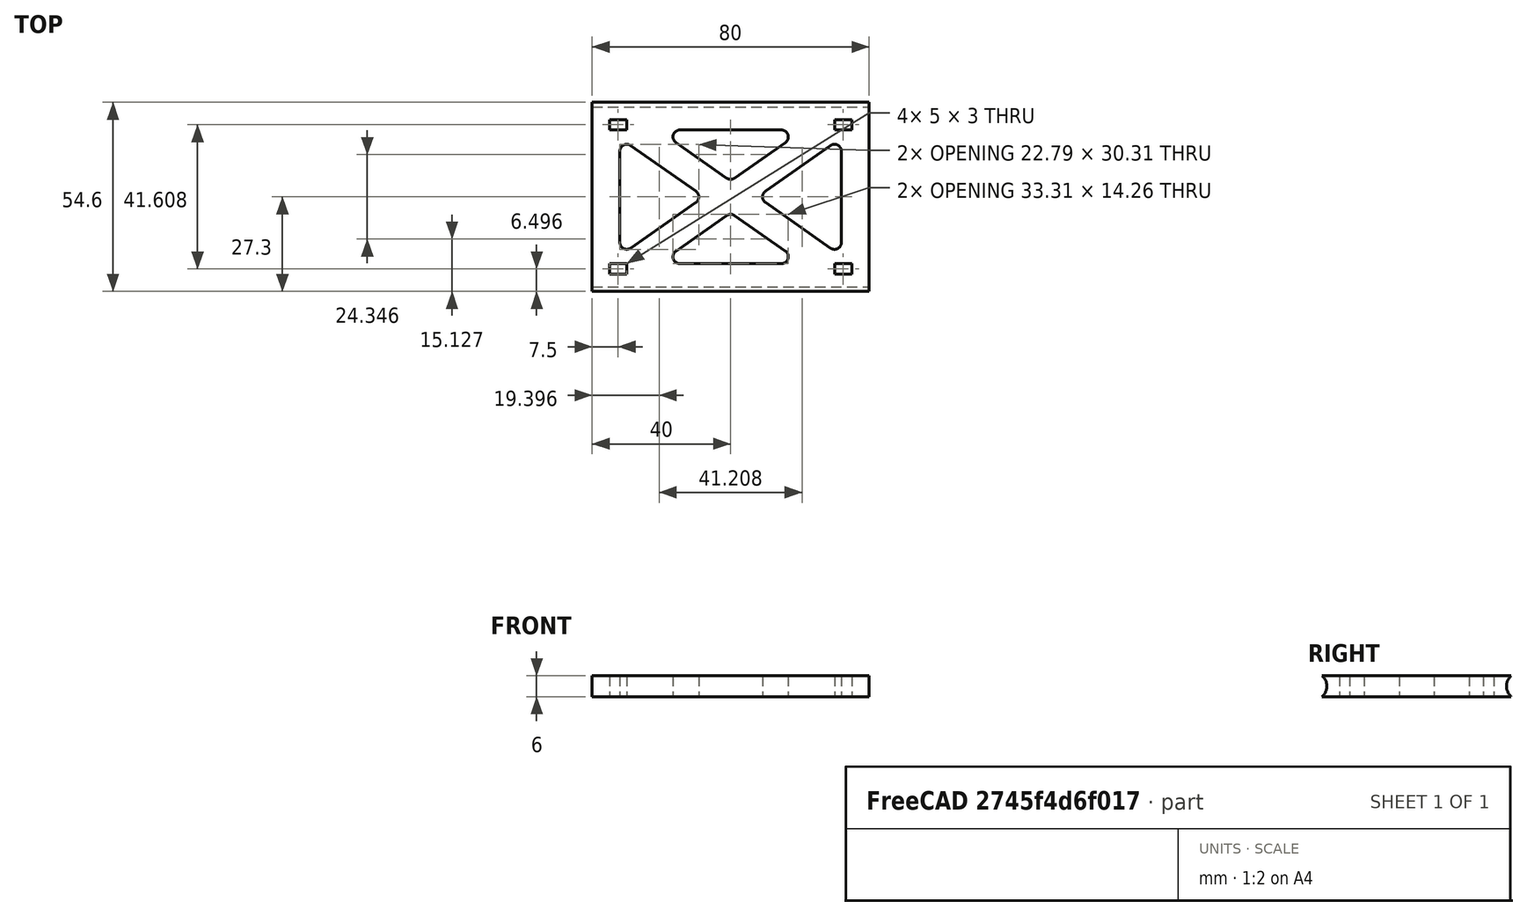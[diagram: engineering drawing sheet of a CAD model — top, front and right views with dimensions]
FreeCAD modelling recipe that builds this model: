
FCSTD DOCUMENT  (FreeCAD 0.15R4527 (Git))
Label: y_reinforcement
License: All rights reserved
LicenseURL: http://en.wikipedia.org/wiki/All_rights_reserved
objects: Part::Fillet×4, Part::Feature×2, Part::Cylinder×2, Mesh::Feature×1, Part::Box×1, Part::MultiFuse×1, Part::Cut×1, Sketcher::SketchObject×1, PartDesign::Pocket×1
note: 14 computed .brp shape members not serialized (recipe doc carries the construction recipe); baked Part::Feature solids carry a one-line shape summary decoded from their .brp

FEATURE [Mesh::Feature] yreinforcment
FEATURE [Part::Feature] yreinforcment001001  label="yreinforcment002"
  shape: bbox 80 x 54.56 x 6 mm, 392 faces, 0 solids (baked)
FEATURE [Part::Box] Box  label="Cubo"
  Height = 6
  Length = 80
  Placement = pos=(0,-1,0) rot=(0,0,1;0rad)
  Width = 56
FEATURE [Part::Cylinder] Cylinder  label="Cilindro"
  Angle = 360
  Height = 82
  Placement = pos=(-1,-2.65,3) rot=(0,1,0;1.5708rad)
  Radius = 4
FEATURE [Part::Cylinder] Cylinder001  label="Cilindro001"
  Angle = 360
  Height = 82
  Placement = pos=(-1,57.25,3) rot=(0,1,0;1.5708rad)
  Radius = 4
FEATURE [Part::MultiFuse] Fusion
  Shapes = -> [Cylinder,Cylinder001]
FEATURE [Part::Cut] Cut
  Base = -> Box
  Tool = -> Fusion
FEATURE [Sketcher::SketchObject] Sketch
  ExternalGeometry = -> [Cut]
  Placement = pos=(0,0,6) rot=(0,0,1;0rad)
  Support = -> Cut [Face2]
  sketch-geometry (48):
    g0: LineSegment StartX=5 StartY=4.99575 StartZ=0 EndX=10 EndY=4.99575 EndZ=0
    g1: LineSegment StartX=10 StartY=4.99575 StartZ=0 EndX=10 EndY=7.99575 EndZ=0
    g2: LineSegment StartX=10 StartY=7.99575 StartZ=0 EndX=5 EndY=7.99575 EndZ=0
    g3: LineSegment StartX=5 StartY=7.99575 StartZ=0 EndX=5 EndY=4.99575 EndZ=0
    g4: LineSegment [constr] StartX=5 StartY=4.99575 StartZ=0 EndX=5 EndY=-0.00424869 EndZ=0
    g5: LineSegment [constr] StartX=5 StartY=7.99575 StartZ=0 EndX=0 EndY=7.99575 EndZ=0
    g6: LineSegment StartX=5 StartY=49.6042 StartZ=0 EndX=10 EndY=49.6042 EndZ=0
    g7: LineSegment StartX=10 StartY=49.6042 StartZ=0 EndX=10 EndY=46.6042 EndZ=0
    g8: LineSegment StartX=10 StartY=46.6042 StartZ=0 EndX=5 EndY=46.6042 EndZ=0
    g9: LineSegment StartX=5 StartY=46.6042 StartZ=0 EndX=5 EndY=49.6042 EndZ=0
    g10: LineSegment [constr] StartX=5 StartY=46.6042 StartZ=0 EndX=0 EndY=46.6042 EndZ=0
    g11: LineSegment [constr] StartX=5 StartY=49.6042 StartZ=0 EndX=5 EndY=54.6042 EndZ=0
    g12: LineSegment StartX=70 StartY=49.6042 StartZ=0 EndX=75 EndY=49.6042 EndZ=0
    g13: LineSegment StartX=75 StartY=49.6042 StartZ=0 EndX=75 EndY=46.6042 EndZ=0
    g14: LineSegment StartX=75 StartY=46.6042 StartZ=0 EndX=70 EndY=46.6042 EndZ=0
    g15: LineSegment StartX=70 StartY=46.6042 StartZ=0 EndX=70 EndY=49.6042 EndZ=0
    g16: LineSegment [constr] StartX=75 StartY=46.6042 StartZ=0 EndX=80 EndY=46.6042 EndZ=0
    g17: LineSegment [constr] StartX=75 StartY=49.6042 StartZ=0 EndX=75 EndY=54.6042 EndZ=0
    g18: LineSegment StartX=70 StartY=7.99575 StartZ=0 EndX=75 EndY=7.99575 EndZ=0
    g19: LineSegment StartX=75 StartY=7.99575 StartZ=0 EndX=75 EndY=4.99575 EndZ=0
    g20: LineSegment StartX=75 StartY=4.99575 StartZ=0 EndX=70 EndY=4.99575 EndZ=0
    g21: LineSegment StartX=70 StartY=4.99575 StartZ=0 EndX=70 EndY=7.99575 EndZ=0
    g22: LineSegment [constr] StartX=75 StartY=7.99575 StartZ=0 EndX=80 EndY=7.99575 EndZ=0
    g23: LineSegment [constr] StartX=75 StartY=4.99575 StartZ=0 EndX=75 EndY=-0.00424869 EndZ=0
    g24: LineSegment StartX=8 StartY=44.3 StartZ=0 EndX=8 EndY=10.3 EndZ=0
    g25: LineSegment StartX=8 StartY=10.3 StartZ=0 EndX=32.2785 EndY=27.3 EndZ=0
    g26: LineSegment StartX=32.2785 StartY=27.3 StartZ=0 EndX=8 EndY=44.3 EndZ=0
    g27: LineSegment StartX=19 StartY=46.6042 StartZ=0 EndX=61 EndY=46.6042 EndZ=0
    g28: LineSegment StartX=61 StartY=46.6042 StartZ=0 EndX=40 EndY=31.8999 EndZ=0
    g29: LineSegment StartX=40 StartY=31.8999 StartZ=0 EndX=19 EndY=46.6042 EndZ=0
    g30: LineSegment StartX=47.7215 StartY=27.3 StartZ=0 EndX=72 EndY=44.3 EndZ=0
    g31: LineSegment StartX=72 StartY=44.3 StartZ=0 EndX=72 EndY=10.3 EndZ=0
    g32: LineSegment StartX=72 StartY=10.3 StartZ=0 EndX=47.7215 EndY=27.3 EndZ=0
    g33: LineSegment StartX=19 StartY=7.99575 StartZ=0 EndX=61 EndY=7.99575 EndZ=0
    g34: LineSegment StartX=61 StartY=7.99575 StartZ=0 EndX=40 EndY=22.7001 EndZ=0
    g35: LineSegment StartX=40 StartY=22.7001 StartZ=0 EndX=19 EndY=7.99575 EndZ=0
    g36: LineSegment [constr] StartX=8 StartY=44.3 StartZ=0 EndX=8 EndY=46.6042 EndZ=0
    g37: LineSegment [constr] StartX=8 StartY=10.3 StartZ=0 EndX=8 EndY=7.99575 EndZ=0
    g38: LineSegment [constr] StartX=10 StartY=46.6042 StartZ=0 EndX=19 EndY=46.6042 EndZ=0
    g39: LineSegment [constr] StartX=61 StartY=46.6042 StartZ=0 EndX=70 EndY=46.6042 EndZ=0
    g40: LineSegment [constr] StartX=32.2785 StartY=31.8999 StartZ=0 EndX=47.7215 EndY=31.8999 EndZ=0
    g41: LineSegment [constr] StartX=47.7215 StartY=31.8999 StartZ=0 EndX=47.7215 EndY=22.7001 EndZ=0
    g42: LineSegment [constr] StartX=47.7215 StartY=22.7001 StartZ=0 EndX=32.2785 EndY=22.7001 EndZ=0
    g43: LineSegment [constr] StartX=32.2785 StartY=22.7001 StartZ=0 EndX=32.2785 EndY=31.8999 EndZ=0
    g44: LineSegment [constr] StartX=10 StartY=7.99575 StartZ=0 EndX=19 EndY=7.99575 EndZ=0
    g45: LineSegment [constr] StartX=61 StartY=7.99575 StartZ=0 EndX=70 EndY=7.99575 EndZ=0
    g46: LineSegment [constr] StartX=72 StartY=44.3 StartZ=0 EndX=72 EndY=46.6042 EndZ=0
    g47: LineSegment [constr] StartX=72 StartY=10.3 StartZ=0 EndX=72 EndY=7.99575 EndZ=0
  constraints (139):
    c: Coincident(g0,g1)
    c: Coincident(g1,g2)
    c: Coincident(g2,g3)
    c: Coincident(g3,g0)
    c: Horizontal(g0)
    c: Horizontal(g2)
    c: Vertical(g1)
    c: Vertical(g3)
    c: DistanceX(g2) = -5
    c: DistanceY(g1) = 3
    c: Coincident(g4,g0)
    c: PointOnObject(g4,g-3)
    c: Vertical(g4)
    c: Coincident(g5,g2)
    c: PointOnObject(g5,g-4)
    c: Horizontal(g5)
    c: Equal(g5,g4)
    c: Equal(g5,g2)
    c: Coincident(g6,g7)
    c: Coincident(g7,g8)
    c: Coincident(g8,g9)
    c: Coincident(g9,g6)
    c: Horizontal(g6)
    c: Horizontal(g8)
    c: Vertical(g7)
    c: Vertical(g9)
    c: Coincident(g10,g8)
    c: PointOnObject(g10,g-4)
    c: Horizontal(g10)
    c: Coincident(g11,g6)
    c: PointOnObject(g11,g-5)
    c: Vertical(g11)
    c: Equal(g11,g8)
    c: Equal(g8,g10)
    c: Equal(g10,g5)
    c: Equal(g1,g9)
    c: Coincident(g12,g13)
    c: Coincident(g13,g14)
    c: Coincident(g14,g15)
    c: Coincident(g15,g12)
    c: Horizontal(g12)
    c: Horizontal(g14)
    c: Vertical(g13)
    c: Vertical(g15)
    c: Coincident(g16,g13)
    c: PointOnObject(g16,g-6)
    c: Horizontal(g16)
    c: Coincident(g17,g12)
    c: PointOnObject(g17,g-5)
    c: Vertical(g17)
    c: Coincident(g18,g19)
    c: Coincident(g19,g20)
    c: Coincident(g20,g21)
    c: Coincident(g21,g18)
    c: Horizontal(g18)
    c: Horizontal(g20)
    c: Vertical(g19)
    c: Vertical(g21)
    c: Coincident(g22,g18)
    c: PointOnObject(g22,g-6)
    c: Horizontal(g22)
    c: Coincident(g23,g19)
    c: PointOnObject(g23,g-3)
    c: Vertical(g23)
    c: Equal(g23,g20)
    c: Equal(g20,g22)
    c: Equal(g22,g16)
    c: Equal(g16,g12)
    c: Equal(g12,g17)
    c: Equal(g17,g11)
    c: Equal(g15,g21)
    c: Equal(g21,g1)
    c: Vertical(g24)
    c: Coincident(g24,g25)
    c: Coincident(g25,g26)
    c: Coincident(g26,g24)
    c: Horizontal(g27)
    c: Coincident(g27,g28)
    c: Coincident(g28,g29)
    c: Coincident(g29,g27)
    c: Coincident(g30,g31)
    c: Vertical(g31)
    c: Coincident(g31,g32)
    c: Coincident(g32,g30)
    c: Horizontal(g33)
    c: Coincident(g33,g34)
    c: Coincident(g34,g35)
    c: Coincident(g35,g33)
    c: Parallel(g35,g25)
    c: Parallel(g25,g28)
    c: Parallel(g28,g30)
    c: Parallel(g32,g29)
    c: Parallel(g29,g34)
    c: Parallel(g34,g26)
    c: Angle(g24,g26) = 0.959931
    c: Angle(g25,g24) = 0.959931
    c: Coincident(g36,g24)
    c: Vertical(g36)
    c: PointOnObject(g36,g8)
    c: Coincident(g37,g24)
    c: PointOnObject(g37,g2)
    c: Vertical(g37)
    c: DistanceX(g36,g7) = 2
    c: Coincident(g38,g7)
    c: Coincident(g38,g27)
    c: Horizontal(g38)
    c: Coincident(g39,g27)
    c: Coincident(g39,g14)
    c: Coincident(g40,g41)
    c: Coincident(g41,g42)
    c: Coincident(g42,g43)
    c: Horizontal(g40)
    c: Horizontal(g42)
    c: Vertical(g41)
    c: Vertical(g43)
    c: Coincident(g44,g1)
    c: Coincident(g44,g33)
    c: Horizontal(g44)
    c: Coincident(g45,g33)
    c: Coincident(g45,g18)
    c: Equal(g44,g45)
    c: Equal(g37,g36)
    c: Symmetric(g40,g42,g25)
    c: Symmetric(g40,g40,g28)
    c: Symmetric(g42,g41,g34)
    c: Symmetric(g41,g40,g30)
    c: Equal(g38,g39)
    c: Equal(g39,g45)
    c: Coincident(g46,g30)
    c: PointOnObject(g46,g14)
    c: Vertical(g46)
    c: Coincident(g47,g31)
    c: PointOnObject(g47,g18)
    c: Vertical(g47)
    c: Equal(g47,g46)
    c: Equal(g46,g36)
    c: Coincident(g43,g40)
    c: DistanceY(g24) = -34
    c: DistanceX(g27) = 42
FEATURE [PartDesign::Pocket] Pocket
  Length = 5
  Sketch = -> Sketch
  Type = 1
FEATURE [Part::Fillet] Fillet
  Base = -> Pocket
  Edges = 4 edges r=2: [Edge84,Edge86,Edge87,Edge89]
FEATURE [Part::Fillet] Fillet001
  Base = -> Fillet
  Edges = 4 edges r=2: [Edge71,Edge73,Edge93,Edge97]
FEATURE [Part::Fillet] Fillet002
  Base = -> Fillet001
  Edges = 2 edges r=2: [Edge48,Edge112]
FEATURE [Part::Fillet] Fillet003  label="y_reinforcement"
  Base = -> Fillet002
  Edges = 2 edges r=2: [Edge56,Edge106]
FEATURE [Part::Feature] Fillet004  label="y_reinforcement001"
  shape: bbox 80 x 54.61 x 6 mm, 46 faces (baked)
